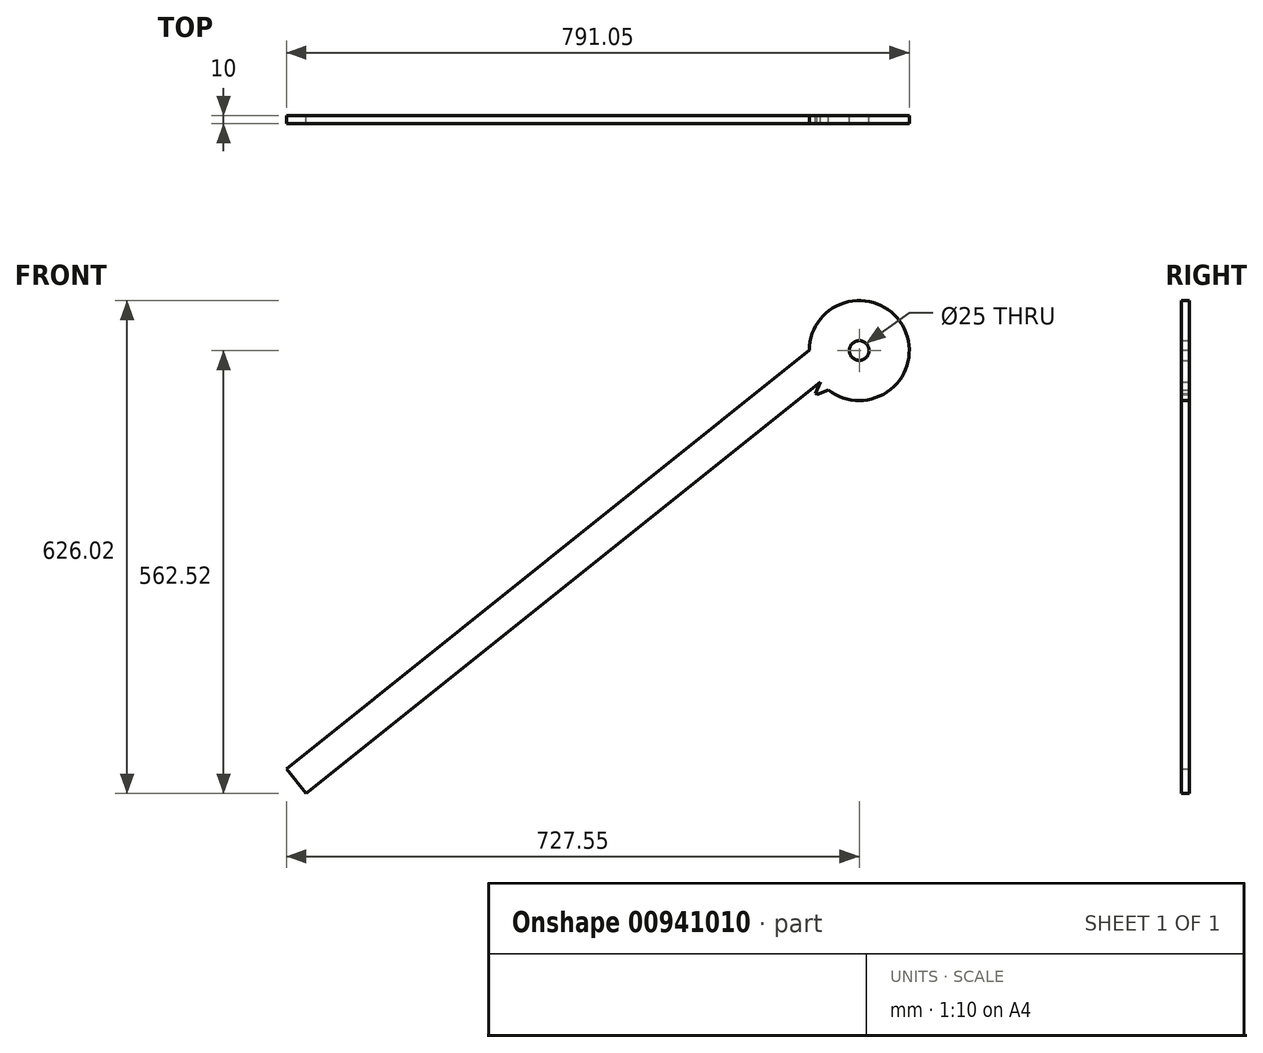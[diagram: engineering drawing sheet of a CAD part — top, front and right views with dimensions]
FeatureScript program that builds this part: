
annotation { "Feature Type Name" : "Feature", "Feature Type Description" : "" }
export const myFeature = defineFeature(function(context is Context, id is Id, definition is map)
    precondition{}
    {
        {
            var Q0;
            Q0=qCreatedBy(makeId("Front.planeOp"),FACE);
            var sketch = newSketch(context, id + "F0", { "sketchPlane" : qUnion([Q0])});
            skCircle(sketch, "E0", {"center": v(0, 0) * mm, "radius": 63.5 * mm});
            skLineSegment(sketch, "E1", {"start": v(0, 0) * mm, "end": v(-49.57, -39.69) * mm});
            skLineSegment(sketch, "E2", {"start": v(0, 0) * mm, "end": v(62.77, 9.59) * mm});
            skLineSegment(sketch, "E3", {"start": v(-49.57, -39.69) * mm, "end": v(-55.72, -54.35) * mm});
            skLineSegment(sketch, "E4", {"start": v(-55.72, -54.35) * mm, "end": v(-53.94, -56.12) * mm});
            skLineSegment(sketch, "E5", {"start": v(-53.94, -56.12) * mm, "end": v(-39.32, -49.86) * mm});
            skLineSegment(sketch, "E6", {"start": v(0, 0) * mm, "end": v(-702.55, -562.52) * mm});
            skLineSegment(sketch, "E7", {"start": v(-702.55, -562.52) * mm, "end": v(-727.55, -531.3) * mm});
            skLineSegment(sketch, "E8", {"start": v(-727.55, -531.3) * mm, "end": v(-25, 31.22) * mm});
            skLineSegment(sketch, "E9", {"start": v(-25, 31.22) * mm, "end": v(0, 0) * mm});
            skSolve(sketch);
        }
        {
            var Q0;
            {var subQ0=sQuery(id+"F0.wireOp",EDGE,"E1");Q0=makeQuery(id+"F0.imprint","IMPRINT",FACE,{"disambiguationData":[TD([[makeQuery(id+"F0.imprint","IMPRINT",EDGE,{"derivedFrom":subQ0}),-1.0]])]});}
            var Q1;
            {var subQ0=sQuery(id+"F0.wireOp",EDGE,"E2");Q1=makeQuery(id+"F0.imprint","IMPRINT",FACE,{"disambiguationData":[TD([[makeQuery(id+"F0.imprint","IMPRINT",EDGE,{"derivedFrom":subQ0}),1.0]])]});}
            var Q2;
            {var subQ0=sQuery(id+"F0.wireOp",EDGE,"E1");Q2=makeQuery(id+"F0.imprint","IMPRINT",FACE,{"disambiguationData":[TD([[makeQuery(id+"F0.imprint","IMPRINT",EDGE,{"derivedFrom":subQ0}),1.0]])]});}
            var Q3;
            {var subQ0=sQuery(id+"F0.wireOp",EDGE,"E6");Q3=makeQuery(id+"F0.imprint","IMPRINT",FACE,{"disambiguationData":[TD([[makeQuery(id+"F0.imprint","IMPRINT",EDGE,{"derivedFrom":subQ0}),-1.0]])]});}
            extrude(context, id + "F1", {"entities" : qUnion([Q0, Q1, Q2, Q3]), "endBound" : BoundingType.SYMMETRIC, "depth" : 10 * mm, "offsetDistance" : 25 * mm});
        }
        {
            var Q0;
            {var subQ0=sQuery(id+"F0.wireOp",EDGE,"E3");Q0=makeQuery(id+"F0.imprint","IMPRINT",FACE,{"disambiguationData":[TD([[makeQuery(id+"F0.imprint","IMPRINT",EDGE,{"derivedFrom":subQ0}),1.0]])]});}
            extrude(context, id + "F2", {"entities" : qUnion([Q0]), "operationType" : NewBodyOperationType.ADD, "endBound" : BoundingType.SYMMETRIC, "depth" : 10 * mm, "offsetDistance" : 25 * mm});
        }
        {
            var Q0;
            {var subQ0=sQuery(id+"F0.wireOp",EDGE,"E5");var subQ1=sQuery(id+"F0.wireOp",EDGE,"E4");var subQ2=sQuery(id+"F0.wireOp",EDGE,"E3");var subQ3=sQuery(id+"F0.wireOp",EDGE,"E0");Q0=makeQuery(id+"F4V7WTG4KkVU04k_1.10.F2.boolean.opBoolean","MERGE",FACE,{"derivedFrom":[makeQuery(id+"F4V7WTG4KkVU04k_1.9.F2.boolean.opBoolean","MERGE",FACE,{"derivedFrom":[makeQuery(id+"F4V7WTG4KkVU04k_1.8.F2.boolean.opBoolean","MERGE",FACE,{"derivedFrom":[makeQuery(id+"F4V7WTG4KkVU04k_1.7.F2.boolean.opBoolean","MERGE",FACE,{"derivedFrom":[makeQuery(id+"F4V7WTG4KkVU04k_1.6.F2.boolean.opBoolean","MERGE",FACE,{"derivedFrom":[makeQuery(id+"F4V7WTG4KkVU04k_1.5.F2.boolean.opBoolean","MERGE",FACE,{"derivedFrom":[makeQuery(id+"F4V7WTG4KkVU04k_1.4.F2.boolean.opBoolean","MERGE",FACE,{"derivedFrom":[makeQuery(id+"F4V7WTG4KkVU04k_1.3.F2.boolean.opBoolean","MERGE",FACE,{"derivedFrom":[makeQuery(id+"F4V7WTG4KkVU04k_1.2.F2.boolean.opBoolean","MERGE",FACE,{"derivedFrom":[makeQuery(id+"F4V7WTG4KkVU04k_1.1.F2.boolean.opBoolean","MERGE",FACE,{"derivedFrom":[makeQuery(id+"F2.boolean.opBoolean","MERGE",FACE,{"derivedFrom":[makeQuery(id+"F1.opExtrude","CAP_FACE",FACE,{"disambiguationData":[OSD([subQ3,sQuery(id+"F0.wireOp",EDGE,"E6"),sQuery(id+"F0.wireOp",EDGE,"E7"),sQuery(id+"F0.wireOp",EDGE,"E8")])],"isStart":true}),makeQuery(id+"F2.opExtrude","CAP_FACE",FACE,{"disambiguationData":[OSD([subQ3,subQ2,subQ1,subQ0])],"isStart":true})]}),makeQuery(id+"F4V7WTG4KkVU04k_1.1.F2.opExtrude","CAP_FACE",FACE,{"disambiguationData":[OSD([subQ3,subQ2,subQ1,subQ0])],"isStart":true})]}),makeQuery(id+"F4V7WTG4KkVU04k_1.2.F2.opExtrude","CAP_FACE",FACE,{"disambiguationData":[OSD([subQ3,subQ2,subQ1,subQ0])],"isStart":true})]}),makeQuery(id+"F4V7WTG4KkVU04k_1.3.F2.opExtrude","CAP_FACE",FACE,{"disambiguationData":[OSD([subQ3,subQ2,subQ1,subQ0])],"isStart":true})]}),makeQuery(id+"F4V7WTG4KkVU04k_1.4.F2.opExtrude","CAP_FACE",FACE,{"disambiguationData":[OSD([subQ3,subQ2,subQ1,subQ0])],"isStart":true})]}),makeQuery(id+"F4V7WTG4KkVU04k_1.5.F2.opExtrude","CAP_FACE",FACE,{"disambiguationData":[OSD([subQ3,subQ2,subQ1,subQ0])],"isStart":true})]}),makeQuery(id+"F4V7WTG4KkVU04k_1.6.F2.opExtrude","CAP_FACE",FACE,{"disambiguationData":[OSD([subQ3,subQ2,subQ1,subQ0])],"isStart":true})]}),makeQuery(id+"F4V7WTG4KkVU04k_1.7.F2.opExtrude","CAP_FACE",FACE,{"disambiguationData":[OSD([subQ3,subQ2,subQ1,subQ0])],"isStart":true})]}),makeQuery(id+"F4V7WTG4KkVU04k_1.8.F2.opExtrude","CAP_FACE",FACE,{"disambiguationData":[OSD([subQ3,subQ2,subQ1,subQ0])],"isStart":true})]}),makeQuery(id+"F4V7WTG4KkVU04k_1.9.F2.opExtrude","CAP_FACE",FACE,{"disambiguationData":[OSD([subQ3,subQ2,subQ1,subQ0])],"isStart":true})]}),makeQuery(id+"F4V7WTG4KkVU04k_1.10.F2.opExtrude","CAP_FACE",FACE,{"disambiguationData":[OSD([subQ3,subQ2,subQ1,subQ0])],"isStart":true})]});}
            var sketch = newSketch(context, id + "F3", { "sketchPlane" : qUnion([Q0])});
            skCircle(sketch, "E10", {"center": v(0, 0) * mm, "radius": 12.5 * mm});
            skSolve(sketch);
        }
        {
            var Q0;
            Q0 = qSketchRegion(id + "F3", true);
            extrude(context, id + "F4", {"entities" : qUnion([Q0]), "operationType" : NewBodyOperationType.REMOVE, "endBound" : BoundingType.THROUGH_ALL, "oppositeDirection" : true, "depth" : 25 * mm, "offsetDistance" : 25 * mm});
        }
    });
